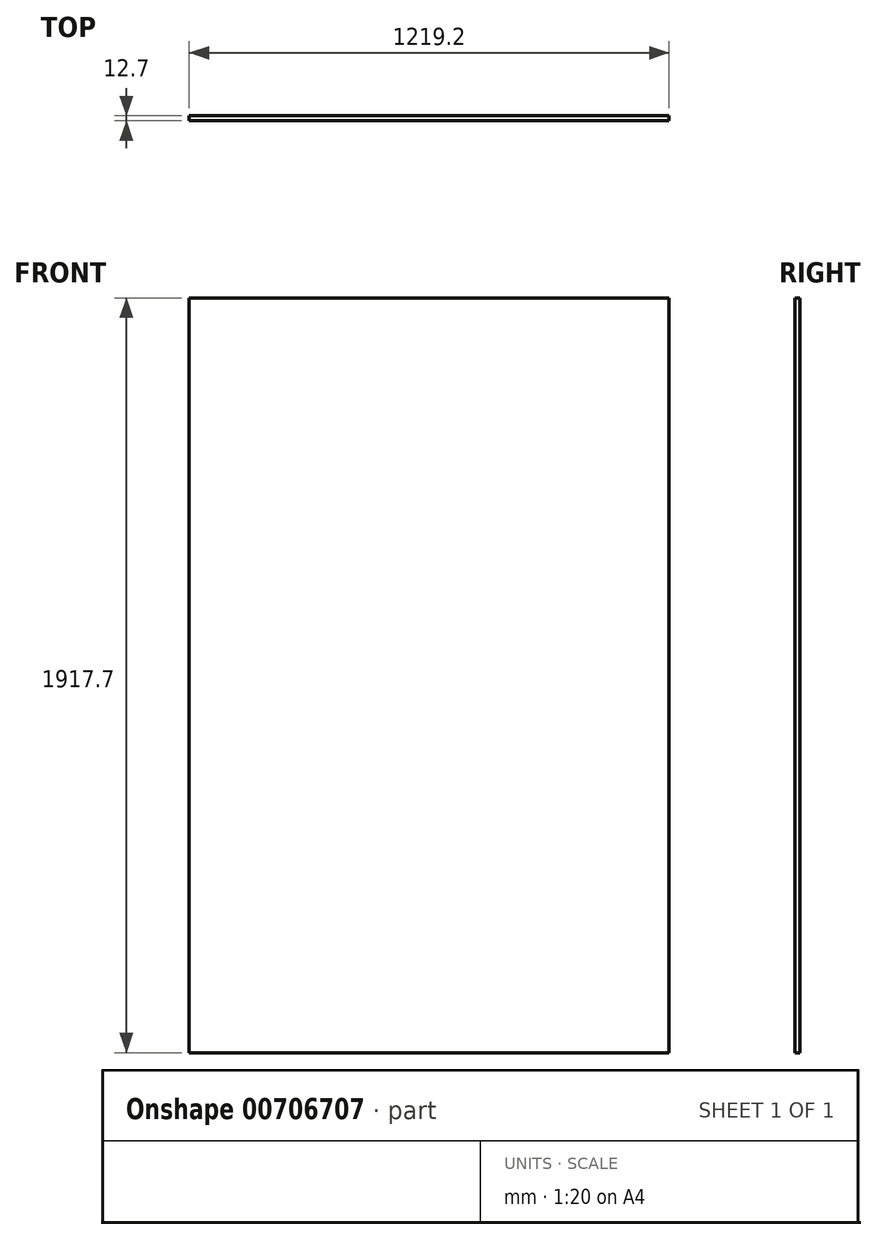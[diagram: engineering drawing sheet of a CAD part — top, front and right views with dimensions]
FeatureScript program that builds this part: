
annotation { "Feature Type Name" : "Feature", "Feature Type Description" : "" }
export const myFeature = defineFeature(function(context is Context, id is Id, definition is map)
    precondition{}
    {
        {
            var Q0;
            Q0=qCreatedBy(makeId("Front.planeOp"),FACE);
            var sketch = newSketch(context, id + "F0", { "sketchPlane" : qUnion([Q0])});
            skLineSegment(sketch, "E0.bottom", {"start": v(0, 0) * mm, "end": v(1219.2, 0) * mm});
            skLineSegment(sketch, "E0.top", {"start": v(0, 1917.7) * mm, "end": v(1219.2, 1917.7) * mm});
            skLineSegment(sketch, "E0.left", {"start": v(0, 0) * mm, "end": v(0, 1917.7) * mm});
            skLineSegment(sketch, "E0.right", {"start": v(1219.2, 0) * mm, "end": v(1219.2, 1917.7) * mm});
            skSolve(sketch);
        }
        {
            var Q0;
            Q0=makeQuery(id+"F0.imprint","IMPRINT",FACE,{"disambiguationData":[TD([[makeQuery(id+"F0.imprint","IMPRINT",EDGE,{"derivedFrom":sQuery(id+"F0.wireOp",EDGE,"E0.bottom")}),1.0]])]});
            extrude(context, id + "F1", {"entities" : qUnion([Q0]), "depth" : 12.7 * mm, "offsetDistance" : 25.4 * mm});
        }
    });
